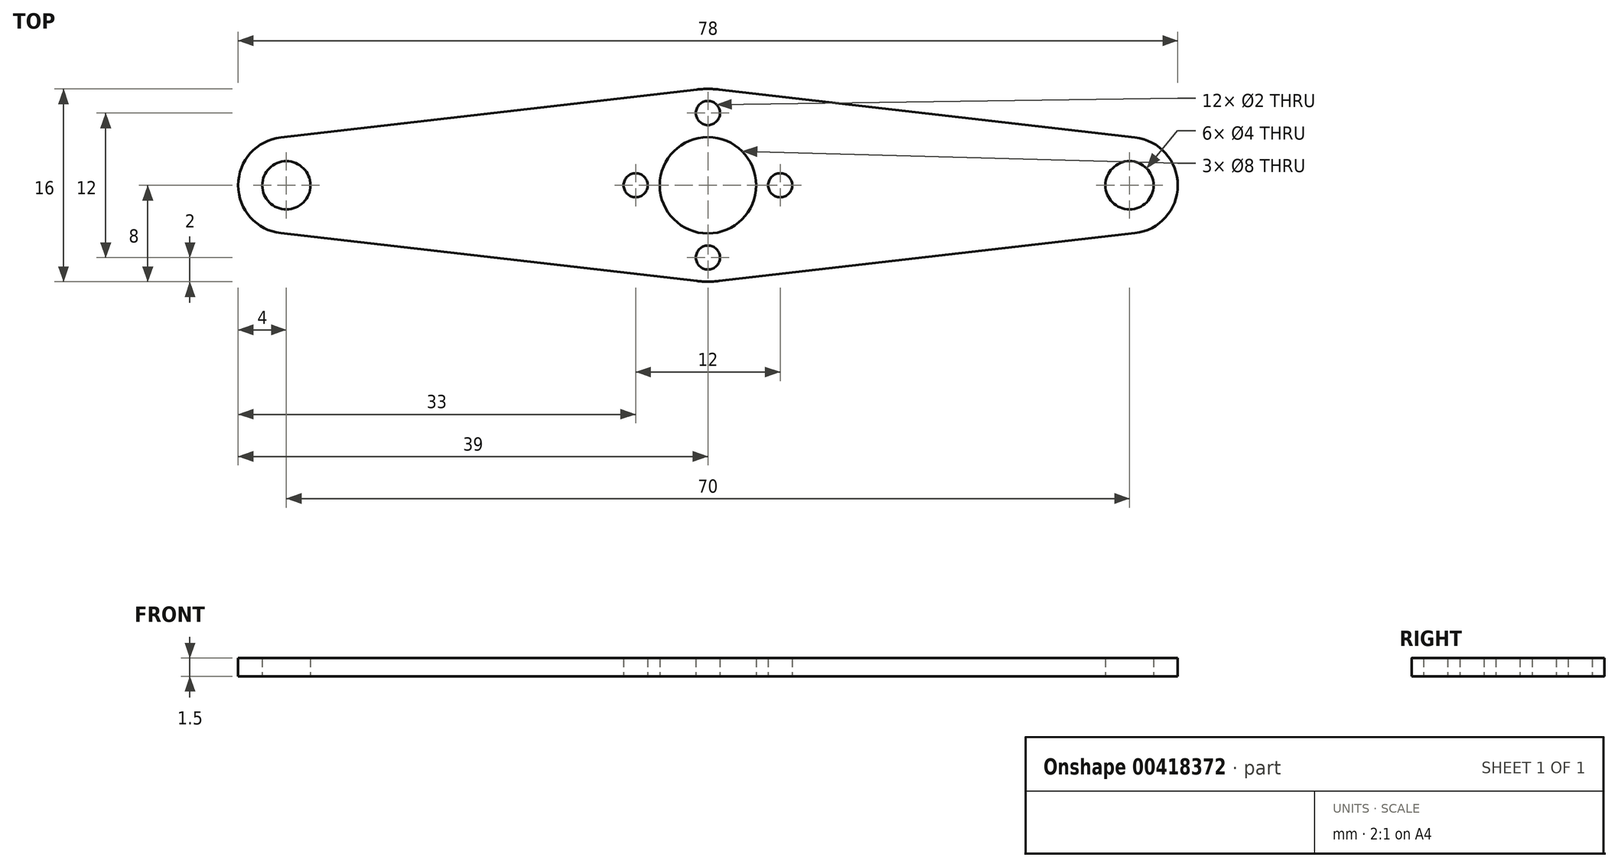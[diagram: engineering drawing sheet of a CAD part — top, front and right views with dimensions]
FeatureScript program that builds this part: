
annotation { "Feature Type Name" : "Feature", "Feature Type Description" : "" }
export const myFeature = defineFeature(function(context is Context, id is Id, definition is map)
    precondition{}
    {
        {
            var Q0;
            Q0=qCreatedBy(makeId("Top.planeOp"),FACE);
            var sketch = newSketch(context, id + "F0", { "sketchPlane" : qUnion([Q0])});
            skCircle(sketch, "E0", {"center": v(35, 0) * mm, "radius": 2 * mm});
            skCircle(sketch, "E1", {"center": v(0, 0) * mm, "radius": 4 * mm});
            skCircle(sketch, "E2", {"center": v(0, 6) * mm, "radius": 1 * mm});
            skArc(sketch, "E3", {"start": v(35.46, -3.97) * mm, "mid": v(39, 0) * mm, "end": v(35.46, 3.97) * mm});
            skCircle(sketch, "E4.1.0", {"center": v(-6, 0) * mm, "radius": 1 * mm});
            skCircle(sketch, "E4.2.0", {"center": v(0, -6) * mm, "radius": 1 * mm});
            skCircle(sketch, "E5.1.3.0", {"center": v(6, 0) * mm, "radius": 1 * mm});
            skArc(sketch, "E6.MirrorC", {"start": v(-35.46, -3.97) * mm, "mid": v(-39, 0) * mm, "end": v(-35.46, 3.97) * mm});
            skCircle(sketch, "E7.MirrorC", {"center": v(-35, 0) * mm, "radius": 2 * mm});
            skArc(sketch, "E8", {"start": v(0.91, 7.95) * mm, "mid": v(0, 8) * mm, "end": v(-0.91, 7.95) * mm});
            skLineSegment(sketch, "E9", {"start": v(0.91, 7.95) * mm, "end": v(35.46, 3.97) * mm});
            skLineSegment(sketch, "E10.MirrorCS", {"start": v(0.91, -7.95) * mm, "end": v(35.46, -3.97) * mm});
            skLineSegment(sketch, "E11.MirrorCS", {"start": v(-0.91, 7.95) * mm, "end": v(-35.46, 3.97) * mm});
            skLineSegment(sketch, "E12.MirrorCS", {"start": v(-0.91, -7.95) * mm, "end": v(-35.46, -3.97) * mm});
            skArc(sketch, "E13.trimOffspring", {"start": v(-0.91, -7.95) * mm, "mid": v(0, -8) * mm, "end": v(0.91, -7.95) * mm});
            skSolve(sketch);
        }
        {
            var Q0;
            Q0 = qSketchRegion(id + "F0", true);
            extrude(context, id + "F1", {"entities" : qUnion([Q0]), "depth" : 1.5 * mm, "offsetDistance" : 25 * mm});
        }
    });
